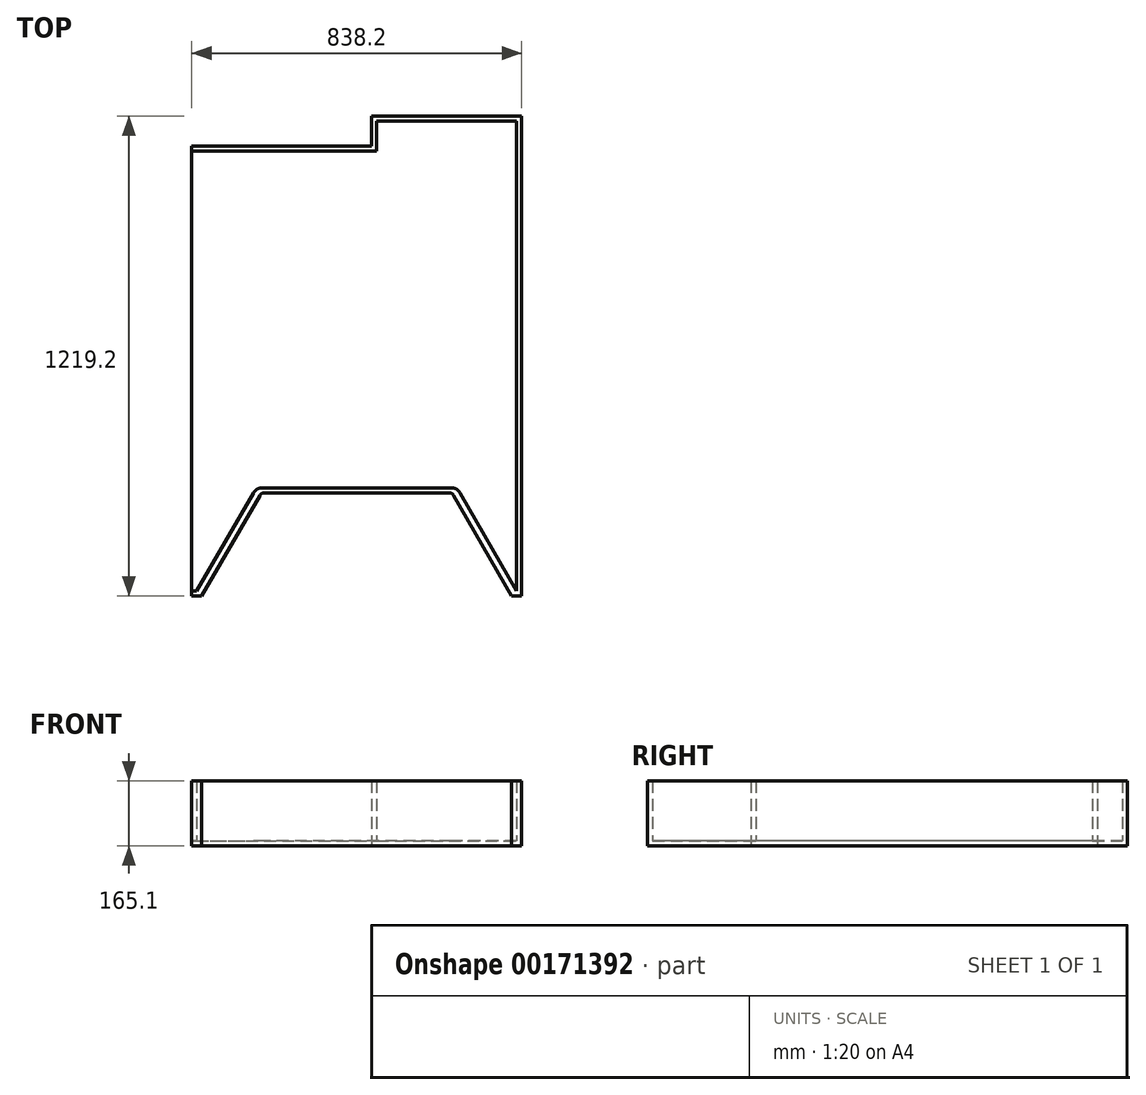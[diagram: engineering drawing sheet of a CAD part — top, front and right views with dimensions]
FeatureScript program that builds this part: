
annotation { "Feature Type Name" : "Feature", "Feature Type Description" : "" }
export const myFeature = defineFeature(function(context is Context, id is Id, definition is map)
    precondition{}
    {
        {
            var Q0;
            Q0=qCreatedBy(makeId("Top.planeOp"),FACE);
            var sketch = newSketch(context, id + "F0", { "sketchPlane" : qUnion([Q0])});
            skLineSegment(sketch, "E0", {"start": v(368.3, -361.93) * mm, "end": v(368.3, 857.27) * mm});
            skLineSegment(sketch, "E1", {"start": v(368.3, 857.27) * mm, "end": v(-12.7, 857.27) * mm});
            skLineSegment(sketch, "E2", {"start": v(-12.7, 857.27) * mm, "end": v(-12.7, 781.07) * mm});
            skLineSegment(sketch, "E3", {"start": v(-12.7, 781.07) * mm, "end": v(-469.9, 781.07) * mm});
            skLineSegment(sketch, "E4", {"start": v(-469.9, 781.07) * mm, "end": v(-469.9, -361.93) * mm});
            skLineSegment(sketch, "E5", {"start": v(-457.2, 768.37) * mm, "end": v(0, 768.37) * mm});
            skLineSegment(sketch, "E6", {"start": v(0, 768.37) * mm, "end": v(0, 819.17) * mm});
            skPoint(sketch, "E6.endSnap0", {"position": v(-12.7, 819.17) * mm});
            skLineSegment(sketch, "E7", {"start": v(355.6, 844.57) * mm, "end": v(355.6, -349.23) * mm});
            skLineSegment(sketch, "E8", {"start": v(-457.2, 768.37) * mm, "end": v(-457.2, -349.23) * mm});
            skLineSegment(sketch, "E9", {"start": v(0, 819.17) * mm, "end": v(0, 844.57) * mm});
            skLineSegment(sketch, "E10", {"start": v(0, 844.57) * mm, "end": v(355.6, 844.57) * mm});
            skLineSegment(sketch, "E11", {"start": v(-469.9, -361.93) * mm, "end": v(368.3, -361.93) * mm, "construction": true});
            skLineSegment(sketch, "E12", {"start": v(-444.5, -361.93) * mm, "end": v(-297.06, -106.55) * mm});
            skLineSegment(sketch, "E13", {"start": v(-286.06, -100.2) * mm, "end": v(184.46, -100.2) * mm});
            skLineSegment(sketch, "E14", {"start": v(195.46, -106.55) * mm, "end": v(342.9, -361.93) * mm});
            skLineSegment(sketch, "E15", {"start": v(-457.2, -349.23) * mm, "end": v(-313.42, -100.2) * mm});
            skLineSegment(sketch, "E16", {"start": v(355.6, -349.23) * mm, "end": v(211.82, -100.2) * mm});
            skLineSegment(sketch, "E17", {"start": v(189.83, -87.5) * mm, "end": v(-291.43, -87.5) * mm});
            skPoint(sketch, "E18.visualSharp", {"position": v(-306.1, -87.5) * mm});
            skArc(sketch, "E18.filletArc", {"start": v(-291.43, -87.5) * mm, "mid": v(-304.13, -90.9) * mm, "end": v(-313.42, -100.2) * mm});
            skPoint(sketch, "E19.visualSharp", {"position": v(204.5, -87.5) * mm});
            skArc(sketch, "E19.filletArc", {"start": v(211.82, -100.2) * mm, "mid": v(202.53, -90.9) * mm, "end": v(189.83, -87.5) * mm});
            skPoint(sketch, "E20.visualSharp", {"position": v(-293.4, -100.2) * mm});
            skArc(sketch, "E20.filletArc", {"start": v(-286.06, -100.2) * mm, "mid": v(-292.4, -101.9) * mm, "end": v(-297.06, -106.55) * mm});
            skPoint(sketch, "E21.visualSharp", {"position": v(191.8, -100.2) * mm});
            skArc(sketch, "E21.filletArc", {"start": v(195.46, -106.55) * mm, "mid": v(190.8, -101.9) * mm, "end": v(184.46, -100.2) * mm});
            skLineSegment(sketch, "E22", {"start": v(-469.9, -361.93) * mm, "end": v(-444.5, -361.93) * mm});
            skLineSegment(sketch, "E23", {"start": v(342.9, -361.93) * mm, "end": v(368.3, -361.93) * mm});
            skLineSegment(sketch, "E24", {"start": v(-457.2, 768.37) * mm, "end": v(-469.9, 768.37) * mm});
            skLineSegment(sketch, "E25", {"start": v(-457.2, -349.23) * mm, "end": v(-469.9, -349.23) * mm});
            skSolve(sketch);
        }
        {
            var Q0;
            Q0=makeQuery(id+"F0.imprint","IMPRINT",FACE,{"disambiguationData":[TD([[makeQuery(id+"F0.imprint","IMPRINT",EDGE,{"derivedFrom":sQuery(id+"F0.wireOp",EDGE,"E0")}),1.0]])]});
            extrude(context, id + "F1", {"entities" : qUnion([Q0]), "depth" : 165.1 * mm});
        }
        {
            var Q0;
            Q0=makeQuery(id+"F0.imprint","IMPRINT",FACE,{"disambiguationData":[TD([[makeQuery(id+"F0.imprint","IMPRINT",EDGE,{"derivedFrom":sQuery(id+"F0.wireOp",EDGE,"E5")}),-1.0]])]});
            extrude(context, id + "F2", {"entities" : qUnion([Q0]), "operationType" : NewBodyOperationType.ADD, "depth" : 12.7 * mm});
        }
        {
            var Q0;
            Q0=makeQuery(id+"F0.imprint","IMPRINT",FACE,{"disambiguationData":[TD([[makeQuery(id+"F0.imprint","IMPRINT",EDGE,{"derivedFrom":sQuery(id+"F0.wireOp",EDGE,"E8")}),-1.0]])]});
            extrude(context, id + "F3", {"entities" : qUnion([Q0]), "operationType" : NewBodyOperationType.ADD, "depth" : 12.7 * mm});
        }
    });
